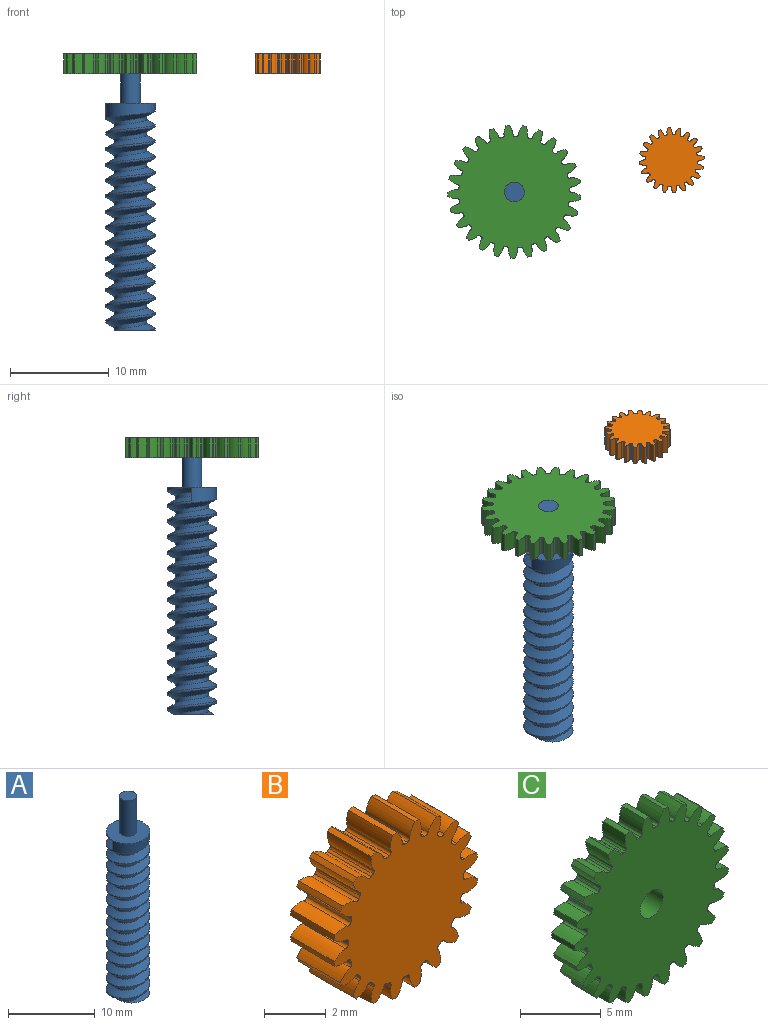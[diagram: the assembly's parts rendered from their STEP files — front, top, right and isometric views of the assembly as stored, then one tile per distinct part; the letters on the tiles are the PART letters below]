
ASSEMBLY  parts=3 mates=3
PART A: 9 faces, bbox 5.4x5.4x29 mm
  f0: cylinder r=2.5mm len=23mm, axis (0,0,-1), area 52.8mm2, adj f1,f2,f3,f5,f6
  f1: plane 4.55x4.48mm, normal (0,0,-1), area 13.1mm2, adj f0,f3,f4,f5
  f2: plane 5x5mm, normal (0,0,1), area 16.5mm2, adj f0,f7
  f3: bspline ~23.5x5mm, area 185.9mm2, adj f0,f1,f4,f6
  f4: cylinder r=1.64mm len=22.5mm, axis (0,0,1), area 42.6mm2, adj f1,f3,f5,f6
  f5: bspline ~22.73x5.02mm, area 178.4mm2, adj f0,f1,f4,f6
  f6: plane 1.39x0.86mm, normal (0,1,0), area 0.8mm2, adj f0,f3,f4,f5
  f7: cylinder r=1mm len=5mm, axis (0,0,-1), area 31.4mm2, adj f2,f8
  f8: plane 2x2mm, normal (0,0,1), area 3.1mm2, adj f7
PART B: 122 faces, bbox 6.6x2x6.6 mm
  f0: cylinder r=3.3mm len=2mm, axis (0,1,0), area 0.4mm2, adj f19,f21,f72,f119
  f1: cylinder r=3.3mm len=2mm, axis (0,1,0), area 0.4mm2, adj f19,f21,f114,f117
  f2: cylinder r=3.3mm len=2mm, axis (0,1,0), area 0.4mm2, adj f19,f21,f109,f112
  f3: cylinder r=3.3mm len=2mm, axis (0,1,0), area 0.4mm2, adj f19,f21,f104,f107
  f4: cylinder r=3.3mm len=2mm, axis (0,1,0), area 0.4mm2, adj f19,f21,f99,f102
  f5: cylinder r=3.3mm len=2mm, axis (0,1,0), area 0.4mm2, adj f19,f21,f94,f97
  f6: cylinder r=3.3mm len=2mm, axis (0,1,0), area 0.4mm2, adj f19,f21,f89,f92
  f7: cylinder r=3.3mm len=2mm, axis (0,1,0), area 0.4mm2, adj f19,f21,f84,f87
  f8: cylinder r=3.3mm len=2mm, axis (0,1,0), area 0.4mm2, adj f19,f21,f67,f79
  f9: cylinder r=3.3mm len=2mm, axis (0,1,0), area 0.4mm2, adj f19,f21,f74,f77
  f10: cylinder r=3.3mm len=2mm, axis (0,1,0), area 0.4mm2, adj f19,f21,f62,f69
  f11: cylinder r=3.3mm len=2mm, axis (0,1,0), area 0.4mm2, adj f19,f21,f42,f64
  f12: cylinder r=3.3mm len=2mm, axis (0,1,0), area 0.4mm2, adj f19,f21,f22,f59
  f13: cylinder r=3.3mm len=2mm, axis (0,1,0), area 0.4mm2, adj f19,f21,f54,f57
  f14: cylinder r=3.3mm len=2mm, axis (0,1,0), area 0.4mm2, adj f19,f21,f49,f52
  f15: cylinder r=3.3mm len=2mm, axis (0,1,0), area 0.4mm2, adj f19,f21,f44,f47
  f16: cylinder r=3.3mm len=2mm, axis (0,1,0), area 0.4mm2, adj f19,f21,f32,f39
  f17: cylinder r=3.3mm len=2mm, axis (0,1,0), area 0.4mm2, adj f19,f21,f34,f82
  f18: cylinder r=3.3mm len=2mm, axis (0,1,0), area 0.4mm2, adj f19,f21,f29,f37
  f19: plane 6.55x6.55mm, normal (0,-1,0), area 27.7mm2, adj f0,f1,f2,f3,f4,f5,f6,f7
  f20: cylinder r=3.3mm len=2mm, axis (0,1,0), area 0.4mm2, adj f19,f21,f24,f27
  f21: plane 6.55x6.55mm, normal (0,1,0), area 27.7mm2, adj f0,f1,f2,f3,f4,f5,f6,f7
  f22: extruded ~2x0.54mm, area 1.2mm2, adj f12,f19,f21,f25
  f23: cylinder r=2.62mm len=2mm, axis (0,1,0), area 0.2mm2, adj f19,f21,f25,f26
  f24: extruded ~2x0.54mm, area 1.2mm2, adj f19,f20,f21,f26
  f25: cylinder r=0.12mm len=2mm, axis (0,1,0), area 0.4mm2, adj f19,f21,f22,f23
  f26: cylinder r=0.12mm len=2mm, axis (0,1,0), area 0.4mm2, adj f19,f21,f23,f24
  f27: extruded ~2x0.59mm, area 1.2mm2, adj f19,f20,f21,f30
  f28: cylinder r=2.62mm len=2mm, axis (0,1,0), area 0.2mm2, adj f19,f21,f30,f31
  f29: extruded ~2x0.44mm, area 1.2mm2, adj f18,f19,f21,f31
  f30: cylinder r=0.12mm len=2mm, axis (0,1,0), area 0.4mm2, adj f19,f21,f27,f28
  f31: cylinder r=0.12mm len=2mm, axis (0,1,0), area 0.4mm2, adj f19,f21,f28,f29
  f32: extruded ~2x0.51mm, area 1.2mm2, adj f16,f19,f21,f35
  f33: cylinder r=2.62mm len=2mm, axis (0,1,0), area 0.2mm2, adj f19,f21,f35,f36
  f34: extruded ~2x0.58mm, area 1.2mm2, adj f17,f19,f21,f36
  f35: cylinder r=0.12mm len=2mm, axis (0,1,0), area 0.4mm2, adj f19,f21,f32,f33
  f36: cylinder r=0.12mm len=2mm, axis (0,1,0), area 0.4mm2, adj f19,f21,f33,f34
  f37: extruded ~2x0.58mm, area 1.2mm2, adj f18,f19,f21,f40
  f38: cylinder r=2.62mm len=2mm, axis (0,1,0), area 0.2mm2, adj f19,f21,f40,f41
  f39: extruded ~2x0.51mm, area 1.2mm2, adj f16,f19,f21,f41
  f40: cylinder r=0.12mm len=2mm, axis (0,1,0), area 0.4mm2, adj f19,f21,f37,f38
  f41: cylinder r=0.12mm len=2mm, axis (0,1,0), area 0.4mm2, adj f19,f21,f38,f39
  f42: extruded ~2x0.59mm, area 1.2mm2, adj f11,f19,f21,f45
  f43: cylinder r=2.62mm len=2mm, axis (0,1,0), area 0.2mm2, adj f19,f21,f45,f46
  f44: extruded ~2x0.44mm, area 1.2mm2, adj f15,f19,f21,f46
  f45: cylinder r=0.12mm len=2mm, axis (0,1,0), area 0.4mm2, adj f19,f21,f42,f43
  f46: cylinder r=0.12mm len=2mm, axis (0,1,0), area 0.4mm2, adj f19,f21,f43,f44
  f47: extruded ~2x0.58mm, area 1.2mm2, adj f15,f19,f21,f50
  f48: cylinder r=2.62mm len=2mm, axis (0,1,0), area 0.2mm2, adj f19,f21,f50,f51
  f49: extruded ~2x0.51mm, area 1.2mm2, adj f14,f19,f21,f51
  f50: cylinder r=0.12mm len=2mm, axis (0,1,0), area 0.4mm2, adj f19,f21,f47,f48
  f51: cylinder r=0.12mm len=2mm, axis (0,1,0), area 0.4mm2, adj f19,f21,f48,f49
  f52: extruded ~2x0.51mm, area 1.2mm2, adj f14,f19,f21,f55
  f53: cylinder r=2.62mm len=2mm, axis (0,1,0), area 0.2mm2, adj f19,f21,f55,f56
  f54: extruded ~2x0.58mm, area 1.2mm2, adj f13,f19,f21,f56
  f55: cylinder r=0.12mm len=2mm, axis (0,1,0), area 0.4mm2, adj f19,f21,f52,f53
  f56: cylinder r=0.12mm len=2mm, axis (0,1,0), area 0.4mm2, adj f19,f21,f53,f54
  f57: extruded ~2x0.44mm, area 1.2mm2, adj f13,f19,f21,f60
  f58: cylinder r=2.62mm len=2mm, axis (0,1,0), area 0.2mm2, adj f19,f21,f60,f61
  f59: extruded ~2x0.59mm, area 1.2mm2, adj f12,f19,f21,f61
  f60: cylinder r=0.12mm len=2mm, axis (0,1,0), area 0.4mm2, adj f19,f21,f57,f58
  f61: cylinder r=0.12mm len=2mm, axis (0,1,0), area 0.4mm2, adj f19,f21,f58,f59
  f62: extruded ~2x0.54mm, area 1.2mm2, adj f10,f19,f21,f65
  f63: cylinder r=2.62mm len=2mm, axis (0,1,0), area 0.2mm2, adj f19,f21,f65,f66
  f64: extruded ~2x0.54mm, area 1.2mm2, adj f11,f19,f21,f66
  f65: cylinder r=0.12mm len=2mm, axis (0,1,0), area 0.4mm2, adj f19,f21,f62,f63
  f66: cylinder r=0.12mm len=2mm, axis (0,1,0), area 0.4mm2, adj f19,f21,f63,f64
  f67: extruded ~2x0.44mm, area 1.2mm2, adj f8,f19,f21,f70
  f68: cylinder r=2.62mm len=2mm, axis (0,1,0), area 0.2mm2, adj f19,f21,f70,f71
  f69: extruded ~2x0.59mm, area 1.2mm2, adj f10,f19,f21,f71
  f70: cylinder r=0.12mm len=2mm, axis (0,1,0), area 0.4mm2, adj f19,f21,f67,f68
  f71: cylinder r=0.12mm len=2mm, axis (0,1,0), area 0.4mm2, adj f19,f21,f68,f69
  f72: extruded ~2x0.58mm, area 1.2mm2, adj f0,f19,f21,f75
  f73: cylinder r=2.62mm len=2mm, axis (0,1,0), area 0.2mm2, adj f19,f21,f75,f76
  f74: extruded ~2x0.51mm, area 1.2mm2, adj f9,f19,f21,f76
  f75: cylinder r=0.12mm len=2mm, axis (0,1,0), area 0.4mm2, adj f19,f21,f72,f73
  f76: cylinder r=0.12mm len=2mm, axis (0,1,0), area 0.4mm2, adj f19,f21,f73,f74
  f77: extruded ~2x0.51mm, area 1.2mm2, adj f9,f19,f21,f80
  f78: cylinder r=2.62mm len=2mm, axis (0,1,0), area 0.2mm2, adj f19,f21,f80,f81
  f79: extruded ~2x0.58mm, area 1.2mm2, adj f8,f19,f21,f81
  f80: cylinder r=0.12mm len=2mm, axis (0,1,0), area 0.4mm2, adj f19,f21,f77,f78
  f81: cylinder r=0.12mm len=2mm, axis (0,1,0), area 0.4mm2, adj f19,f21,f78,f79
  f82: extruded ~2x0.44mm, area 1.2mm2, adj f17,f19,f21,f85
  f83: cylinder r=2.62mm len=2mm, axis (0,1,0), area 0.2mm2, adj f19,f21,f85,f86
  f84: extruded ~2x0.59mm, area 1.2mm2, adj f7,f19,f21,f86
  f85: cylinder r=0.12mm len=2mm, axis (0,1,0), area 0.4mm2, adj f19,f21,f82,f83
  f86: cylinder r=0.12mm len=2mm, axis (0,1,0), area 0.4mm2, adj f19,f21,f83,f84
  f87: extruded ~2x0.54mm, area 1.2mm2, adj f7,f19,f21,f90
  f88: cylinder r=2.62mm len=2mm, axis (0,1,0), area 0.2mm2, adj f19,f21,f90,f91
  f89: extruded ~2x0.54mm, area 1.2mm2, adj f6,f19,f21,f91
  f90: cylinder r=0.12mm len=2mm, axis (0,1,0), area 0.4mm2, adj f19,f21,f87,f88
  f91: cylinder r=0.12mm len=2mm, axis (0,1,0), area 0.4mm2, adj f19,f21,f88,f89
  f92: extruded ~2x0.59mm, area 1.2mm2, adj f6,f19,f21,f95
  f93: cylinder r=2.62mm len=2mm, axis (0,1,0), area 0.2mm2, adj f19,f21,f95,f96
  f94: extruded ~2x0.44mm, area 1.2mm2, adj f5,f19,f21,f96
  f95: cylinder r=0.12mm len=2mm, axis (0,1,0), area 0.4mm2, adj f19,f21,f92,f93
  f96: cylinder r=0.12mm len=2mm, axis (0,1,0), area 0.4mm2, adj f19,f21,f93,f94
  f97: extruded ~2x0.58mm, area 1.2mm2, adj f5,f19,f21,f100
  f98: cylinder r=2.62mm len=2mm, axis (0,1,0), area 0.2mm2, adj f19,f21,f100,f101
  f99: extruded ~2x0.51mm, area 1.2mm2, adj f4,f19,f21,f101
  f100: cylinder r=0.12mm len=2mm, axis (0,1,0), area 0.4mm2, adj f19,f21,f97,f98
  f101: cylinder r=0.12mm len=2mm, axis (0,1,0), area 0.4mm2, adj f19,f21,f98,f99
  f102: extruded ~2x0.51mm, area 1.2mm2, adj f4,f19,f21,f105
  f103: cylinder r=2.62mm len=2mm, axis (0,1,0), area 0.2mm2, adj f19,f21,f105,f106
  f104: extruded ~2x0.58mm, area 1.2mm2, adj f3,f19,f21,f106
  f105: cylinder r=0.12mm len=2mm, axis (0,1,0), area 0.4mm2, adj f19,f21,f102,f103
  f106: cylinder r=0.12mm len=2mm, axis (0,1,0), area 0.4mm2, adj f19,f21,f103,f104
  f107: extruded ~2x0.44mm, area 1.2mm2, adj f3,f19,f21,f110
  f108: cylinder r=2.62mm len=2mm, axis (0,1,0), area 0.2mm2, adj f19,f21,f110,f111
  f109: extruded ~2x0.59mm, area 1.2mm2, adj f2,f19,f21,f111
  f110: cylinder r=0.12mm len=2mm, axis (0,1,0), area 0.4mm2, adj f19,f21,f107,f108
  f111: cylinder r=0.12mm len=2mm, axis (0,1,0), area 0.4mm2, adj f19,f21,f108,f109
  f112: extruded ~2x0.54mm, area 1.2mm2, adj f2,f19,f21,f115
  f113: cylinder r=2.62mm len=2mm, axis (0,1,0), area 0.2mm2, adj f19,f21,f115,f116
  f114: extruded ~2x0.54mm, area 1.2mm2, adj f1,f19,f21,f116
  f115: cylinder r=0.12mm len=2mm, axis (0,1,0), area 0.4mm2, adj f19,f21,f112,f113
  f116: cylinder r=0.12mm len=2mm, axis (0,1,0), area 0.4mm2, adj f19,f21,f113,f114
  f117: extruded ~2x0.59mm, area 1.2mm2, adj f1,f19,f21,f120
  f118: cylinder r=2.62mm len=2mm, axis (0,1,0), area 0.2mm2, adj f19,f21,f120,f121
  f119: extruded ~2x0.44mm, area 1.2mm2, adj f0,f19,f21,f121
  f120: cylinder r=0.12mm len=2mm, axis (0,1,0), area 0.4mm2, adj f19,f21,f117,f118
  f121: cylinder r=0.12mm len=2mm, axis (0,1,0), area 0.4mm2, adj f19,f21,f118,f119
PART C: 153 faces, bbox 13.5x2x13.5 mm
  f0: cylinder r=6.75mm len=2mm, axis (0,1,0), area 0.7mm2, adj f24,f26,f137,f149
  f1: cylinder r=6.75mm len=2mm, axis (0,1,0), area 0.7mm2, adj f24,f26,f144,f147
  f2: cylinder r=6.75mm len=2mm, axis (0,1,0), area 0.7mm2, adj f24,f26,f132,f139
  f3: cylinder r=6.75mm len=2mm, axis (0,1,0), area 0.7mm2, adj f24,f26,f127,f134
  f4: cylinder r=6.75mm len=2mm, axis (0,1,0), area 0.7mm2, adj f24,f26,f122,f129
  f5: cylinder r=6.75mm len=2mm, axis (0,1,0), area 0.7mm2, adj f24,f26,f112,f124
  f6: cylinder r=6.75mm len=2mm, axis (0,1,0), area 0.7mm2, adj f24,f26,f107,f119
  f7: cylinder r=6.75mm len=2mm, axis (0,1,0), area 0.7mm2, adj f24,f26,f114,f117
  f8: cylinder r=6.75mm len=2mm, axis (0,1,0), area 0.7mm2, adj f24,f26,f102,f109
  f9: cylinder r=6.75mm len=2mm, axis (0,1,0), area 0.7mm2, adj f24,f26,f97,f104
  f10: cylinder r=6.75mm len=2mm, axis (0,1,0), area 0.7mm2, adj f24,f26,f92,f99
  f11: cylinder r=6.75mm len=2mm, axis (0,1,0), area 0.7mm2, adj f24,f26,f77,f94
  f12: cylinder r=6.75mm len=2mm, axis (0,1,0), area 0.7mm2, adj f24,f26,f27,f89
  f13: cylinder r=6.75mm len=2mm, axis (0,1,0), area 0.7mm2, adj f24,f26,f84,f87
  f14: cylinder r=6.75mm len=2mm, axis (0,1,0), area 0.7mm2, adj f24,f26,f72,f79
  f15: cylinder r=6.75mm len=2mm, axis (0,1,0), area 0.7mm2, adj f24,f26,f74,f82
  f16: cylinder r=6.75mm len=2mm, axis (0,1,0), area 0.7mm2, adj f24,f26,f69,f142
  f17: cylinder r=6.75mm len=2mm, axis (0,1,0), area 0.7mm2, adj f24,f26,f64,f67
  f18: cylinder r=6.75mm len=2mm, axis (0,1,0), area 0.7mm2, adj f24,f26,f59,f62
  f19: cylinder r=6.75mm len=2mm, axis (0,1,0), area 0.7mm2, adj f24,f26,f54,f57
  f20: cylinder r=6.75mm len=2mm, axis (0,1,0), area 0.7mm2, adj f24,f26,f42,f49
  f21: cylinder r=6.75mm len=2mm, axis (0,1,0), area 0.7mm2, adj f24,f26,f32,f44
  f22: cylinder r=6.75mm len=2mm, axis (0,1,0), area 0.7mm2, adj f24,f26,f39,f52
  f23: cylinder r=6.75mm len=2mm, axis (0,1,0), area 0.7mm2, adj f24,f26,f34,f37
  f24: plane 13.49x13.47mm, normal (0,-1,0), area 117.8mm2, adj f0,f1,f2,f3,f4,f5,f6,f7
  f25: cylinder r=6.75mm len=2mm, axis (0,1,0), area 0.7mm2, adj f24,f26,f29,f47
  f26: plane 13.49x13.47mm, normal (0,1,0), area 117.8mm2, adj f0,f1,f2,f3,f4,f5,f6,f7
  f27: extruded ~2x0.91mm, area 2mm2, adj f12,f24,f26,f30
  f28: cylinder r=5.62mm len=2mm, axis (0,1,0), area 0.3mm2, adj f24,f26,f30,f31
  f29: extruded ~2x0.91mm, area 2mm2, adj f24,f25,f26,f31
  f30: cylinder r=0.19mm len=2mm, axis (0,1,0), area 0.6mm2, adj f24,f26,f27,f28
  f31: cylinder r=0.19mm len=2mm, axis (0,1,0), area 0.6mm2, adj f24,f26,f28,f29
  f32: extruded ~2x0.93mm, area 2mm2, adj f21,f24,f26,f35
  f33: cylinder r=5.62mm len=2mm, axis (0,1,0), area 0.3mm2, adj f24,f26,f35,f36
  f34: extruded ~2x0.91mm, area 2mm2, adj f23,f24,f26,f36
  f35: cylinder r=0.19mm len=2mm, axis (0,1,0), area 0.6mm2, adj f24,f26,f32,f33
  f36: cylinder r=0.19mm len=2mm, axis (0,1,0), area 0.6mm2, adj f24,f26,f33,f34
  f37: extruded ~2x0.82mm, area 2mm2, adj f23,f24,f26,f40
  f38: cylinder r=5.62mm len=2mm, axis (0,1,0), area 0.3mm2, adj f24,f26,f40,f41
  f39: extruded ~2x0.98mm, area 2mm2, adj f22,f24,f26,f41
  f40: cylinder r=0.19mm len=2mm, axis (0,1,0), area 0.6mm2, adj f24,f26,f37,f38
  f41: cylinder r=0.19mm len=2mm, axis (0,1,0), area 0.6mm2, adj f24,f26,f38,f39
  f42: extruded ~2x0.99mm, area 2mm2, adj f20,f24,f26,f45
  f43: cylinder r=5.62mm len=2mm, axis (0,1,0), area 0.3mm2, adj f24,f26,f45,f46
  f44: extruded ~2x0.78mm, area 2mm2, adj f21,f24,f26,f46
  f45: cylinder r=0.19mm len=2mm, axis (0,1,0), area 0.6mm2, adj f24,f26,f42,f43
  f46: cylinder r=0.19mm len=2mm, axis (0,1,0), area 0.6mm2, adj f24,f26,f43,f44
  f47: extruded ~2x0.98mm, area 2mm2, adj f24,f25,f26,f50
  f48: cylinder r=5.62mm len=2mm, axis (0,1,0), area 0.3mm2, adj f24,f26,f50,f51
  f49: extruded ~2x0.79mm, area 2mm2, adj f20,f24,f26,f51
  f50: cylinder r=0.19mm len=2mm, axis (0,1,0), area 0.6mm2, adj f24,f26,f47,f48
  f51: cylinder r=0.19mm len=2mm, axis (0,1,0), area 0.6mm2, adj f24,f26,f48,f49
  f52: extruded ~2x0.75mm, area 2mm2, adj f22,f24,f26,f55
  f53: cylinder r=5.62mm len=2mm, axis (0,1,0), area 0.3mm2, adj f24,f26,f55,f56
  f54: extruded ~2x0.99mm, area 2mm2, adj f19,f24,f26,f56
  f55: cylinder r=0.19mm len=2mm, axis (0,1,0), area 0.6mm2, adj f24,f26,f52,f53
  f56: cylinder r=0.19mm len=2mm, axis (0,1,0), area 0.6mm2, adj f24,f26,f53,f54
  f57: extruded ~2x0.89mm, area 2mm2, adj f19,f24,f26,f60
  f58: cylinder r=5.62mm len=2mm, axis (0,1,0), area 0.3mm2, adj f24,f26,f60,f61
  f59: extruded ~2x0.94mm, area 2mm2, adj f18,f24,f26,f61
  f60: cylinder r=0.19mm len=2mm, axis (0,1,0), area 0.6mm2, adj f24,f26,f57,f58
  f61: cylinder r=0.19mm len=2mm, axis (0,1,0), area 0.6mm2, adj f24,f26,f58,f59
  f62: extruded ~2x0.97mm, area 2mm2, adj f18,f24,f26,f65
  f63: cylinder r=5.62mm len=2mm, axis (0,1,0), area 0.3mm2, adj f24,f26,f65,f66
  f64: extruded ~2x0.82mm, area 2mm2, adj f17,f24,f26,f66
  f65: cylinder r=0.19mm len=2mm, axis (0,1,0), area 0.6mm2, adj f24,f26,f62,f63
  f66: cylinder r=0.19mm len=2mm, axis (0,1,0), area 0.6mm2, adj f24,f26,f63,f64
  f67: extruded ~2x0.99mm, area 2mm2, adj f17,f24,f26,f70
  f68: cylinder r=5.62mm len=2mm, axis (0,1,0), area 0.3mm2, adj f24,f26,f70,f71
  f69: extruded ~2x0.74mm, area 2mm2, adj f16,f24,f26,f71
  f70: cylinder r=0.19mm len=2mm, axis (0,1,0), area 0.6mm2, adj f24,f26,f67,f68
  f71: cylinder r=0.19mm len=2mm, axis (0,1,0), area 0.6mm2, adj f24,f26,f68,f69
  f72: extruded ~2x0.91mm, area 2mm2, adj f14,f24,f26,f75
  f73: cylinder r=5.62mm len=2mm, axis (0,1,0), area 0.3mm2, adj f24,f26,f75,f76
  f74: extruded ~2x0.93mm, area 2mm2, adj f15,f24,f26,f76
  f75: cylinder r=0.19mm len=2mm, axis (0,1,0), area 0.6mm2, adj f24,f26,f72,f73
  f76: cylinder r=0.19mm len=2mm, axis (0,1,0), area 0.6mm2, adj f24,f26,f73,f74
  f77: extruded ~2x0.98mm, area 2mm2, adj f11,f24,f26,f80
  f78: cylinder r=5.62mm len=2mm, axis (0,1,0), area 0.3mm2, adj f24,f26,f80,f81
  f79: extruded ~2x0.82mm, area 2mm2, adj f14,f24,f26,f81
  f80: cylinder r=0.19mm len=2mm, axis (0,1,0), area 0.6mm2, adj f24,f26,f77,f78
  f81: cylinder r=0.19mm len=2mm, axis (0,1,0), area 0.6mm2, adj f24,f26,f78,f79
  f82: extruded ~2x0.78mm, area 2mm2, adj f15,f24,f26,f85
  f83: cylinder r=5.62mm len=2mm, axis (0,1,0), area 0.3mm2, adj f24,f26,f85,f86
  f84: extruded ~2x0.99mm, area 2mm2, adj f13,f24,f26,f86
  f85: cylinder r=0.19mm len=2mm, axis (0,1,0), area 0.6mm2, adj f24,f26,f82,f83
  f86: cylinder r=0.19mm len=2mm, axis (0,1,0), area 0.6mm2, adj f24,f26,f83,f84
  f87: extruded ~2x0.79mm, area 2mm2, adj f13,f24,f26,f90
  f88: cylinder r=5.62mm len=2mm, axis (0,1,0), area 0.3mm2, adj f24,f26,f90,f91
  f89: extruded ~2x0.98mm, area 2mm2, adj f12,f24,f26,f91
  f90: cylinder r=0.19mm len=2mm, axis (0,1,0), area 0.6mm2, adj f24,f26,f87,f88
  f91: cylinder r=0.19mm len=2mm, axis (0,1,0), area 0.6mm2, adj f24,f26,f88,f89
  f92: extruded ~2x0.99mm, area 2mm2, adj f10,f24,f26,f95
  f93: cylinder r=5.62mm len=2mm, axis (0,1,0), area 0.3mm2, adj f24,f26,f95,f96
  f94: extruded ~2x0.75mm, area 2mm2, adj f11,f24,f26,f96
  f95: cylinder r=0.19mm len=2mm, axis (0,1,0), area 0.6mm2, adj f24,f26,f92,f93
  f96: cylinder r=0.19mm len=2mm, axis (0,1,0), area 0.6mm2, adj f24,f26,f93,f94
  f97: extruded ~2x0.94mm, area 2mm2, adj f9,f24,f26,f100
  f98: cylinder r=5.62mm len=2mm, axis (0,1,0), area 0.3mm2, adj f24,f26,f100,f101
  f99: extruded ~2x0.89mm, area 2mm2, adj f10,f24,f26,f101
  f100: cylinder r=0.19mm len=2mm, axis (0,1,0), area 0.6mm2, adj f24,f26,f97,f98
  f101: cylinder r=0.19mm len=2mm, axis (0,1,0), area 0.6mm2, adj f24,f26,f98,f99
  f102: extruded ~2x0.82mm, area 2mm2, adj f8,f24,f26,f105
  f103: cylinder r=5.62mm len=2mm, axis (0,1,0), area 0.3mm2, adj f24,f26,f105,f106
  f104: extruded ~2x0.97mm, area 2mm2, adj f9,f24,f26,f106
  f105: cylinder r=0.19mm len=2mm, axis (0,1,0), area 0.6mm2, adj f24,f26,f102,f103
  f106: cylinder r=0.19mm len=2mm, axis (0,1,0), area 0.6mm2, adj f24,f26,f103,f104
  f107: extruded ~2x0.74mm, area 2mm2, adj f6,f24,f26,f110
  f108: cylinder r=5.62mm len=2mm, axis (0,1,0), area 0.3mm2, adj f24,f26,f110,f111
  f109: extruded ~2x0.99mm, area 2mm2, adj f8,f24,f26,f111
  f110: cylinder r=0.19mm len=2mm, axis (0,1,0), area 0.6mm2, adj f24,f26,f107,f108
  f111: cylinder r=0.19mm len=2mm, axis (0,1,0), area 0.6mm2, adj f24,f26,f108,f109
  f112: extruded ~2x0.97mm, area 2mm2, adj f5,f24,f26,f115
  f113: cylinder r=5.62mm len=2mm, axis (0,1,0), area 0.3mm2, adj f24,f26,f115,f116
  f114: extruded ~2x0.85mm, area 2mm2, adj f7,f24,f26,f116
  f115: cylinder r=0.19mm len=2mm, axis (0,1,0), area 0.6mm2, adj f24,f26,f112,f113
  f116: cylinder r=0.19mm len=2mm, axis (0,1,0), area 0.6mm2, adj f24,f26,f113,f114
  f117: extruded ~2x0.88mm, area 2mm2, adj f7,f24,f26,f120
  f118: cylinder r=5.62mm len=2mm, axis (0,1,0), area 0.3mm2, adj f24,f26,f120,f121
  f119: extruded ~2x0.95mm, area 2mm2, adj f6,f24,f26,f121
  f120: cylinder r=0.19mm len=2mm, axis (0,1,0), area 0.6mm2, adj f24,f26,f117,f118
  f121: cylinder r=0.19mm len=2mm, axis (0,1,0), area 0.6mm2, adj f24,f26,f118,f119
  f122: extruded ~2x0.99mm, area 2mm2, adj f4,f24,f26,f125
  f123: cylinder r=5.62mm len=2mm, axis (0,1,0), area 0.3mm2, adj f24,f26,f125,f126
  f124: extruded ~2x0.71mm, area 2mm2, adj f5,f24,f26,f126
  f125: cylinder r=0.19mm len=2mm, axis (0,1,0), area 0.6mm2, adj f24,f26,f122,f123
  f126: cylinder r=0.19mm len=2mm, axis (0,1,0), area 0.6mm2, adj f24,f26,f123,f124
  f127: extruded ~2x0.95mm, area 2mm2, adj f3,f24,f26,f130
  f128: cylinder r=5.62mm len=2mm, axis (0,1,0), area 0.3mm2, adj f24,f26,f130,f131
  f129: extruded ~2x0.86mm, area 2mm2, adj f4,f24,f26,f131
  f130: cylinder r=0.19mm len=2mm, axis (0,1,0), area 0.6mm2, adj f24,f26,f127,f128
  f131: cylinder r=0.19mm len=2mm, axis (0,1,0), area 0.6mm2, adj f24,f26,f128,f129
  f132: extruded ~2x0.86mm, area 2mm2, adj f2,f24,f26,f135
  f133: cylinder r=5.62mm len=2mm, axis (0,1,0), area 0.3mm2, adj f24,f26,f135,f136
  f134: extruded ~2x0.95mm, area 2mm2, adj f3,f24,f26,f136
  f135: cylinder r=0.19mm len=2mm, axis (0,1,0), area 0.6mm2, adj f24,f26,f132,f133
  f136: cylinder r=0.19mm len=2mm, axis (0,1,0), area 0.6mm2, adj f24,f26,f133,f134
  f137: extruded ~2x0.71mm, area 2mm2, adj f0,f24,f26,f140
  f138: cylinder r=5.62mm len=2mm, axis (0,1,0), area 0.3mm2, adj f24,f26,f140,f141
  f139: extruded ~2x0.99mm, area 2mm2, adj f2,f24,f26,f141
  f140: cylinder r=0.19mm len=2mm, axis (0,1,0), area 0.6mm2, adj f24,f26,f137,f138
  f141: cylinder r=0.19mm len=2mm, axis (0,1,0), area 0.6mm2, adj f24,f26,f138,f139
  f142: extruded ~2x0.95mm, area 2mm2, adj f16,f24,f26,f145
  f143: cylinder r=5.62mm len=2mm, axis (0,1,0), area 0.3mm2, adj f24,f26,f145,f146
  f144: extruded ~2x0.88mm, area 2mm2, adj f1,f24,f26,f146
  f145: cylinder r=0.19mm len=2mm, axis (0,1,0), area 0.6mm2, adj f24,f26,f142,f143
  f146: cylinder r=0.19mm len=2mm, axis (0,1,0), area 0.6mm2, adj f24,f26,f143,f144
  f147: extruded ~2x0.85mm, area 2mm2, adj f1,f24,f26,f150
  f148: cylinder r=5.62mm len=2mm, axis (0,1,0), area 0.3mm2, adj f24,f26,f150,f151
  f149: extruded ~2x0.97mm, area 2mm2, adj f0,f24,f26,f151
  f150: cylinder r=0.19mm len=2mm, axis (0,1,0), area 0.6mm2, adj f24,f26,f147,f148
  f151: cylinder r=0.19mm len=2mm, axis (0,1,0), area 0.6mm2, adj f24,f26,f148,f149
  f152: cylinder r=1mm len=2mm, axis (0,1,0), area 12.6mm2, adj f24,f26
PLACE A t=(-6.26,6.63,2.9)mm fixed
PLACE B rot(axis=(-0.93,-0.26,0.26),94.2deg) t=(9.68,9.82,28.9)mm
PLACE C rot(axis=(-0.21,-0.69,0.69),156.3deg) t=(-6.26,6.63,28.9)mm
MATE planar C.f0 <-> A.f0  axis (0,0,1) through (-6.26,6.63,30.9)mm
MATE planar C.f24 <-> B.f0  axis (0,0,1) through (-0.64,6.93,30.9)mm
MATE cylindrical C.f0 <-> A.f0  axis (0,0,-1) through (-6.26,6.63,30.9)mm
